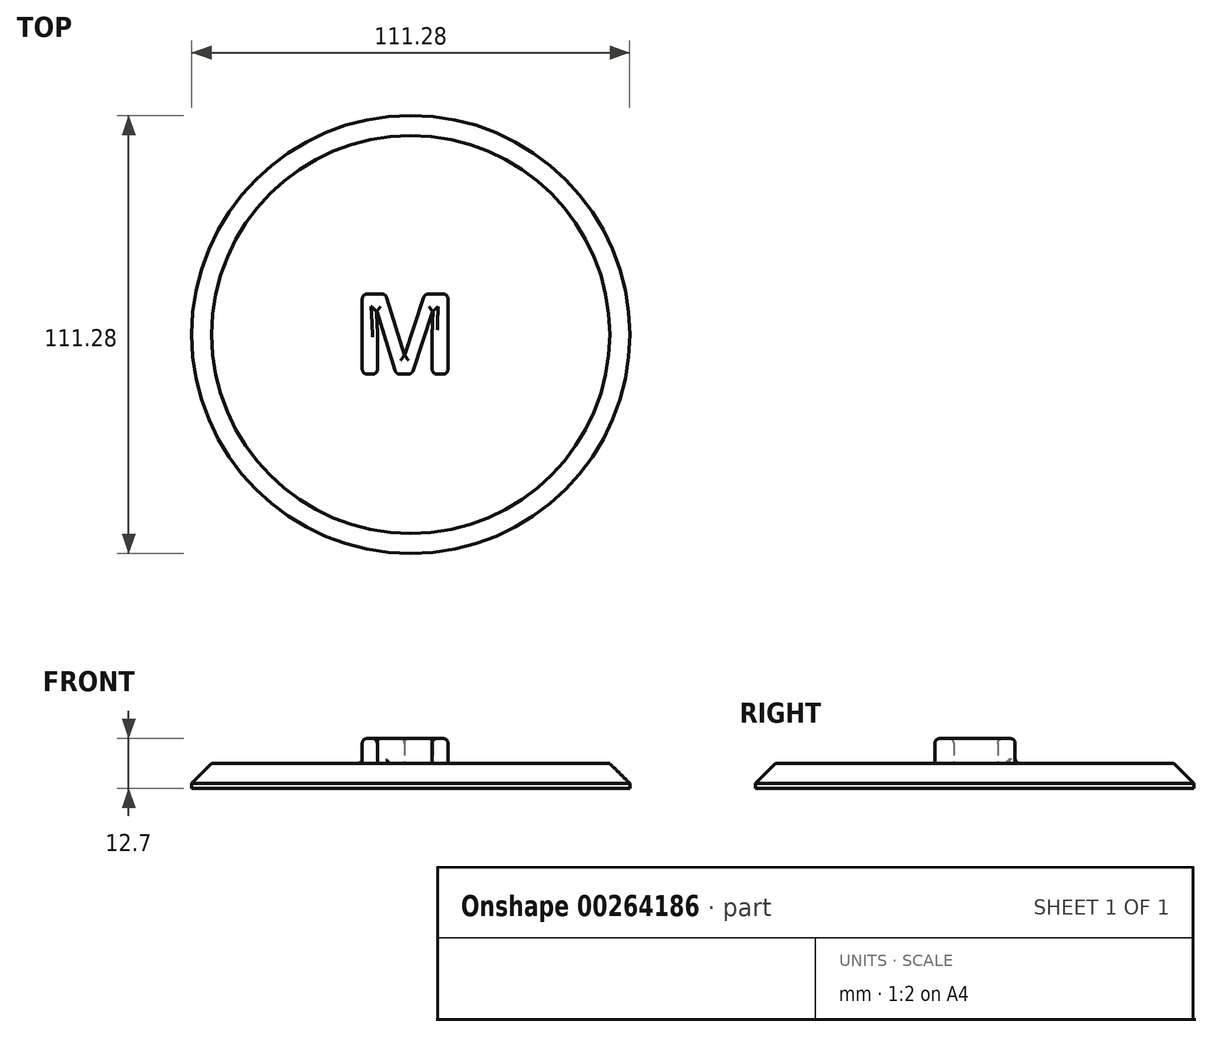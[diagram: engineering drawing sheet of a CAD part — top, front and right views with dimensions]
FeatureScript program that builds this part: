
annotation { "Feature Type Name" : "Feature", "Feature Type Description" : "" }
export const myFeature = defineFeature(function(context is Context, id is Id, definition is map)
    precondition{}
    {
        {
            var Q0;
            Q0=qCreatedBy(makeId("Top.planeOp"),FACE);
            var sketch = newSketch(context, id + "F0", { "sketchPlane" : qUnion([Q0])});
            skCircle(sketch, "E0", {"center": v(0, 0) * mm, "radius": 55.64 * mm});
            skText(sketch, "E1", { "text": "M", "fontName": "OpenSans-Bold.ttf"});
            const initialGuessF0  = {"E1": [-0.01487, -0.0101, 1, 0, 0.02055]};
            skSetInitialGuess(sketch, initialGuessF0);
            skSolve(sketch);
        }
        {
            var Q0;
            Q0=makeQuery(id+"F0.imprint","IMPRINT",FACE,{"disambiguationData":[TD([[makeQuery(id+"F0.imprint","IMPRINT",EDGE,{"derivedFrom":sQuery(id+"F0.wireOp",EDGE,"E1.sketch_text.stroke-0")}),-1.0]])]});
            extrude(context, id + "F1", {"entities" : qUnion([Q0]), "depth" : 12.7 * mm});
        }
        {
            var Q0;
            Q0 = qSketchRegion(id + "F0", true);
            extrude(context, id + "F2", {"entities" : qUnion([Q0]), "operationType" : NewBodyOperationType.ADD, "depth" : 6.35 * mm});
        }
        {
            var Q0;
            Q0=makeQuery(id+"F1.opExtrude","CAP_EDGE",EDGE,{"disambiguationData":[OSD([sQuery(id+"F0.wireOp",EDGE,"E1.sketch_text.stroke-5")])],"isStart":false});
            var Q1;
            Q1=makeQuery(id+"F1.opExtrude","CAP_EDGE",EDGE,{"disambiguationData":[OSD([sQuery(id+"F0.wireOp",EDGE,"E1.sketch_text.stroke-11")])],"isStart":false});
            var Q2;
            Q2=makeQuery(id+"F1.opExtrude","CAP_EDGE",EDGE,{"disambiguationData":[OSD([sQuery(id+"F0.wireOp",EDGE,"E1.sketch_text.stroke-10")])],"isStart":false});
            var Q3;
            Q3=makeQuery(id+"F1.opExtrude","CAP_FACE",FACE,{"disambiguationData":[OSD([sQuery(id+"F0.wireOp",EDGE,"E1.sketch_text.stroke-0"),sQuery(id+"F0.wireOp",EDGE,"E1.sketch_text.stroke-1"),sQuery(id+"F0.wireOp",EDGE,"E1.sketch_text.stroke-2"),sQuery(id+"F0.wireOp",EDGE,"E1.sketch_text.stroke-3"),sQuery(id+"F0.wireOp",EDGE,"E1.sketch_text.stroke-4"),sQuery(id+"F0.wireOp",EDGE,"E1.sketch_text.stroke-5"),sQuery(id+"F0.wireOp",EDGE,"E1.sketch_text.stroke-6"),sQuery(id+"F0.wireOp",EDGE,"E1.sketch_text.stroke-7"),sQuery(id+"F0.wireOp",EDGE,"E1.sketch_text.stroke-8"),sQuery(id+"F0.wireOp",EDGE,"E1.sketch_text.stroke-9"),sQuery(id+"F0.wireOp",EDGE,"E1.sketch_text.stroke-10"),sQuery(id+"F0.wireOp",EDGE,"E1.sketch_text.stroke-11"),sQuery(id+"F0.wireOp",EDGE,"E1.sketch_text.stroke-12"),sQuery(id+"F0.wireOp",EDGE,"E1.sketch_text.stroke-13"),sQuery(id+"F0.wireOp",EDGE,"E1.sketch_text.stroke-14"),sQuery(id+"F0.wireOp",EDGE,"E1.sketch_text.stroke-15"),sQuery(id+"F0.wireOp",EDGE,"E1.sketch_text.stroke-16"),sQuery(id+"F0.wireOp",EDGE,"E1.sketch_text.stroke-17"),sQuery(id+"F0.wireOp",EDGE,"E1.sketch_text.stroke-18")])],"isStart":false});
            var Q4;
            Q4=makeQuery(id+"F1.opExtrude","SWEPT_EDGE",EDGE,{"disambiguationData":[OSD([sQuery(id+"F0.wireOp",EDGE,"E1.sketch_text.stroke-4"),sQuery(id+"F0.wireOp",EDGE,"E1.sketch_text.stroke-5")])]});
            var Q5;
            Q5=makeQuery(id+"F1.opExtrude","SWEPT_EDGE",EDGE,{"disambiguationData":[OSD([sQuery(id+"F0.wireOp",EDGE,"E1.sketch_text.stroke-11"),sQuery(id+"F0.wireOp",EDGE,"E1.sketch_text.stroke-12")])]});
            var Q6;
            Q6=makeQuery(id+"F1.opExtrude","SWEPT_EDGE",EDGE,{"disambiguationData":[OSD([sQuery(id+"F0.wireOp",EDGE,"E1.sketch_text.stroke-3"),sQuery(id+"F0.wireOp",EDGE,"E1.sketch_text.stroke-4")])]});
            var Q7;
            Q7=makeQuery(id+"F1.opExtrude","SWEPT_EDGE",EDGE,{"disambiguationData":[OSD([sQuery(id+"F0.wireOp",EDGE,"E1.sketch_text.stroke-0"),sQuery(id+"F0.wireOp",EDGE,"E1.sketch_text.stroke-18")])]});
            var Q8;
            Q8=makeQuery(id+"F1.opExtrude","SWEPT_EDGE",EDGE,{"disambiguationData":[OSD([sQuery(id+"F0.wireOp",EDGE,"E1.sketch_text.stroke-12"),sQuery(id+"F0.wireOp",EDGE,"E1.sketch_text.stroke-13")])]});
            var Q9;
            Q9=makeQuery(id+"F1.opExtrude","SWEPT_EDGE",EDGE,{"disambiguationData":[OSD([sQuery(id+"F0.wireOp",EDGE,"E1.sketch_text.stroke-17"),sQuery(id+"F0.wireOp",EDGE,"E1.sketch_text.stroke-18")])]});
            var Q10;
            Q10=makeQuery(id+"F1.opExtrude","SWEPT_EDGE",EDGE,{"disambiguationData":[OSD([sQuery(id+"F0.wireOp",EDGE,"E1.sketch_text.stroke-10"),sQuery(id+"F0.wireOp",EDGE,"E1.sketch_text.stroke-11")])]});
            var Q11;
            Q11=makeQuery(id+"F1.opExtrude","SWEPT_EDGE",EDGE,{"disambiguationData":[OSD([sQuery(id+"F0.wireOp",EDGE,"E1.sketch_text.stroke-5"),sQuery(id+"F0.wireOp",EDGE,"E1.sketch_text.stroke-6")])]});
            var Q12;
            Q12=makeQuery(id+"F1.opExtrude","SWEPT_EDGE",EDGE,{"disambiguationData":[OSD([sQuery(id+"F0.wireOp",EDGE,"E1.sketch_text.stroke-9"),sQuery(id+"F0.wireOp",EDGE,"E1.sketch_text.stroke-10")])]});
            var Q13;
            Q13=makeQuery(id+"F1.opExtrude","SWEPT_FACE",FACE,{"disambiguationData":[OSD([sQuery(id+"F0.wireOp",EDGE,"E1.sketch_text.stroke-6")])]});
            fillet(context, id + "F3", {"entities" : qUnion([Q0, Q1, Q2, Q3, Q4, Q5, Q6, Q7, Q8, Q9, Q10, Q11, Q12, Q13]), "radius" : 1.27 * mm, "tangentPropagation" : true, "allowEdgeOverflow" : false});
        }
        {
            var Q0;
            Q0=makeQuery(id+"F2.opExtrude","CAP_EDGE",EDGE,{"disambiguationData":[OSD([sQuery(id+"F0.wireOp",EDGE,"E0")])],"isStart":false});
            chamfer(context, id + "F4", {"entities" : qUnion([Q0]), "width" : 5.08 * mm, "tangentPropagation" : true});
        }
    });
